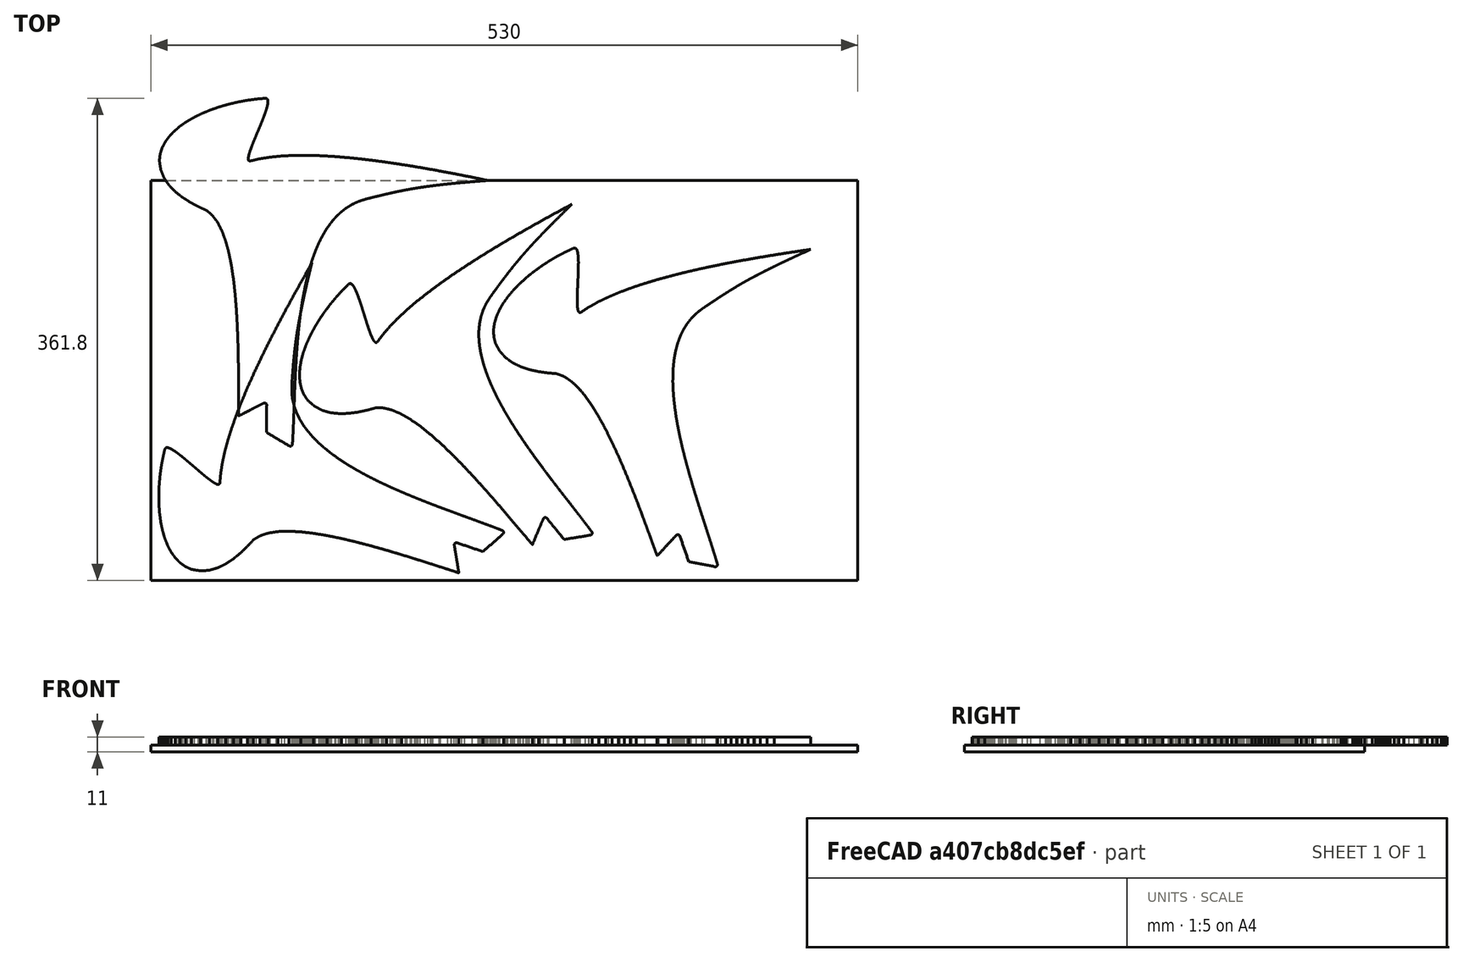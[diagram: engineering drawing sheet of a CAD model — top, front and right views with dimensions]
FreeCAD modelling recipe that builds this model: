
FCSTD DOCUMENT  (FreeCAD 0.17R13327 (Git))
Label: C3
License: All rights reserved
LicenseURL: http://en.wikipedia.org/wiki/All_rights_reserved
objects: Part::Feature×4, App::DocumentObjectGroup×2, Part::Fillet×2, Part::FeaturePython×1, Part::Extrusion×1, Part::Box×1
note: 9 computed .brp shape members not serialized (recipe doc carries the construction recipe); baked Part::Feature solids carry a one-line shape summary decoded from their .brp

FEATURE [Part::Feature] Polyline
  shape: bbox 239.2 x 254.5 x 2e-07 mm, 1 faces, 0 solids (baked)
FEATURE [App::DocumentObjectGroup] _  label="0"
  Group = -> [Polyline]
FEATURE [App::DocumentObjectGroup] C_5b_3  label="C-5b_3"
  Group = -> [_]
FEATURE [Part::FeaturePython] Scale  # Draft clone (typed FeaturePython)
  Objects = -> [Polyline]
  Placement = pos=(573.268,1329.11,0) rot=(0,0,1;0rad)
  Scale = (1.03,1.03,1)
FEATURE [Part::Extrusion] Extrude
  Base = -> Scale
  Dir = (0,0,6)
  DirMode = 0
  FaceMakerClass = Part::FaceMakerExtrusion
  LengthFwd = 0
  LengthRev = 0
  Placement = pos=(-400,-1100,0) rot=(0,0,1;0rad)
  Solid = false
  Symmetric = false
FEATURE [Part::Box] Box  label="machine table"
  AttacherType = Attacher::AttachEngine3D
  Height = 5
  Length = 530
  Placement = pos=(0,0,-5) rot=(0,0,1;0rad)
  Width = 300
FEATURE [Part::Fillet] Fillet
  Base = -> Extrude
  Edges = 1 edges r=1.6: [Edge368]
FEATURE [Part::Fillet] Fillet001
  Base = -> Fillet
  Edges = 1 edges r=1.6: [Edge259]
FEATURE [Part::Feature] Fillet001002  label="Fillet003"
  Placement = pos=(328,-95,0) rot=(0,0,1;1.25664rad)
  shape: bbox 325.4 x 315.3 x 6.734 mm, 129 faces (baked)
FEATURE [Part::Feature] Fillet001003  label="Fillet004"
  Placement = pos=(315,-110,0) rot=(0,0,1;0.698132rad)
  shape: bbox 357.2 x 359.1 x 6.734 mm, 129 faces (baked)
FEATURE [Part::Feature] Fillet001004  label="Fillet005"
  Placement = pos=(360,-120,0) rot=(0,0,1;0.349066rad)
  shape: bbox 321.1 x 330.6 x 6.734 mm, 129 faces (baked)
